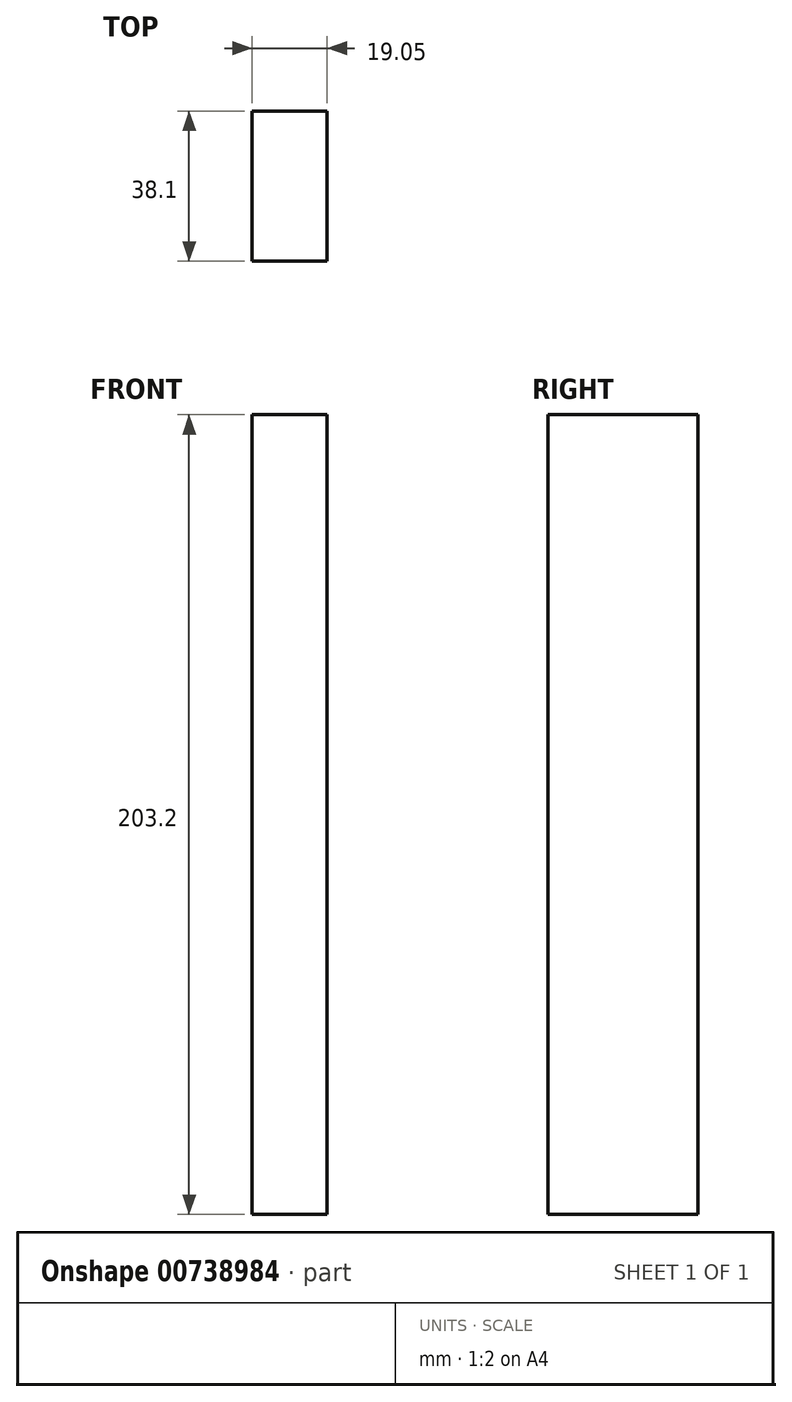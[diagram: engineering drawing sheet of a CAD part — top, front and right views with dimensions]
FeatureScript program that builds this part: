
annotation { "Feature Type Name" : "Feature", "Feature Type Description" : "" }
export const myFeature = defineFeature(function(context is Context, id is Id, definition is map)
    precondition{}
    {
        {
            var Q0;
            Q0=qCreatedBy(makeId("Right.planeOp"),FACE);
            var sketch = newSketch(context, id + "F0", { "sketchPlane" : qUnion([Q0])});
            skLineSegment(sketch, "E0.bottom", {"start": v(-195.13, 0) * mm, "end": v(-157.03, 0) * mm});
            skLineSegment(sketch, "E0.top", {"start": v(-195.13, -203.2) * mm, "end": v(-157.03, -203.2) * mm});
            skLineSegment(sketch, "E0.left", {"start": v(-195.13, 0) * mm, "end": v(-195.13, -203.2) * mm});
            skLineSegment(sketch, "E0.right", {"start": v(-157.03, 0) * mm, "end": v(-157.03, -203.2) * mm});
            skSolve(sketch);
        }
        {
            var Q0;
            Q0=makeQuery(id+"F0.imprint","IMPRINT",FACE,{"disambiguationData":[TD([[makeQuery(id+"F0.imprint","IMPRINT",EDGE,{"derivedFrom":sQuery(id+"F0.wireOp",EDGE,"E0.bottom")}),-1.0]])]});
            extrude(context, id + "F1", {"entities" : qUnion([Q0]), "depth" : 19.05 * mm, "offsetDistance" : 25.4 * mm});
        }
    });
